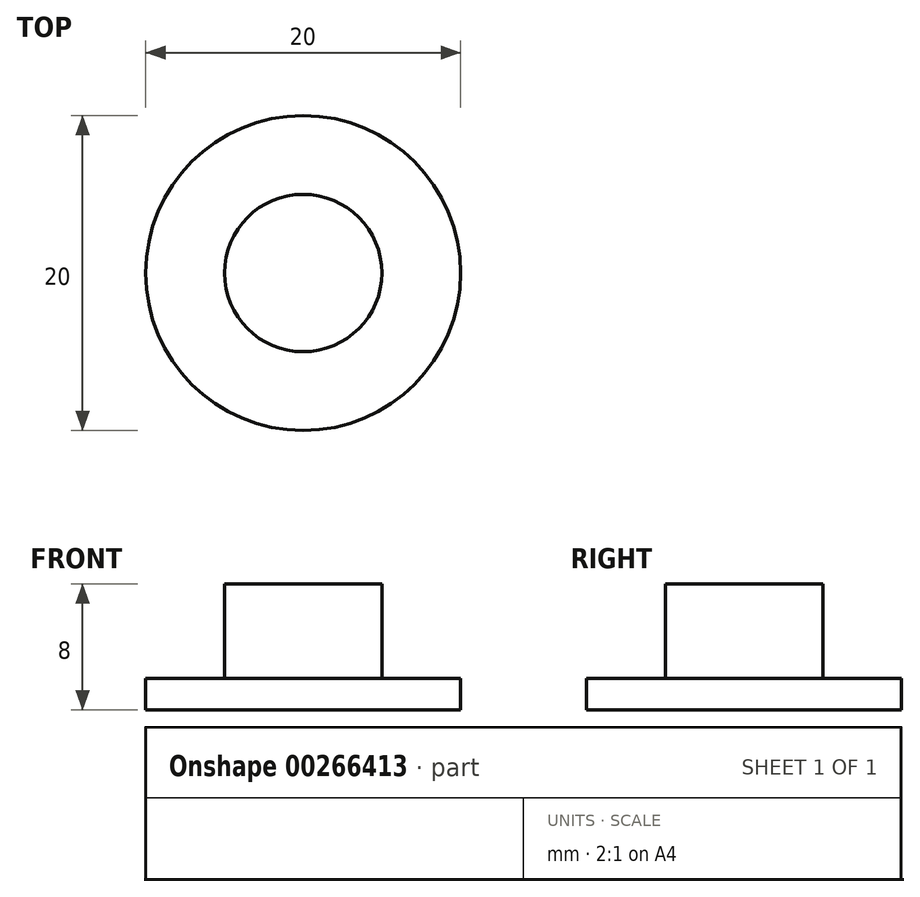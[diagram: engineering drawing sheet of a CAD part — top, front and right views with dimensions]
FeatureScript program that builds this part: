
annotation { "Feature Type Name" : "Feature", "Feature Type Description" : "" }
export const myFeature = defineFeature(function(context is Context, id is Id, definition is map)
    precondition{}
    {
        {
            var Q0;
            Q0=qCreatedBy(makeId("Top.planeOp"),FACE);
            var sketch = newSketch(context, id + "F0", { "sketchPlane" : qUnion([Q0])});
            skCircle(sketch, "E0", {"center": v(0, 0) * mm, "radius": 10 * mm});
            skCircle(sketch, "E1", {"center": v(0, 0) * mm, "radius": 5 * mm});
            skSolve(sketch);
        }
        {
            var Q0;
            Q0=makeQuery(id+"F0.imprint","IMPRINT",FACE,{"disambiguationData":[TD([[makeQuery(id+"F0.imprint","IMPRINT",EDGE,{"derivedFrom":sQuery(id+"F0.wireOp",EDGE,"E0")}),1.0]])]});
            extrude(context, id + "F1", {"entities" : qUnion([Q0]), "depth" : 1 * mm, "hasSecondDirection" : true, "secondDirectionOppositeDirection" : true, "secondDirectionDepth" : 1 * mm});
        }
        {
            var Q0;
            Q0=makeQuery(id+"F0.imprint","IMPRINT",FACE,{"disambiguationData":[TD([[makeQuery(id+"F0.imprint","IMPRINT",EDGE,{"derivedFrom":sQuery(id+"F0.wireOp",EDGE,"E1")}),1.0]])]});
            extrude(context, id + "F2", {"entities" : qUnion([Q0]), "operationType" : NewBodyOperationType.ADD, "depth" : 7 * mm, "hasSecondDirection" : true, "secondDirectionOppositeDirection" : true, "secondDirectionDepth" : 1 * mm});
        }
    });
